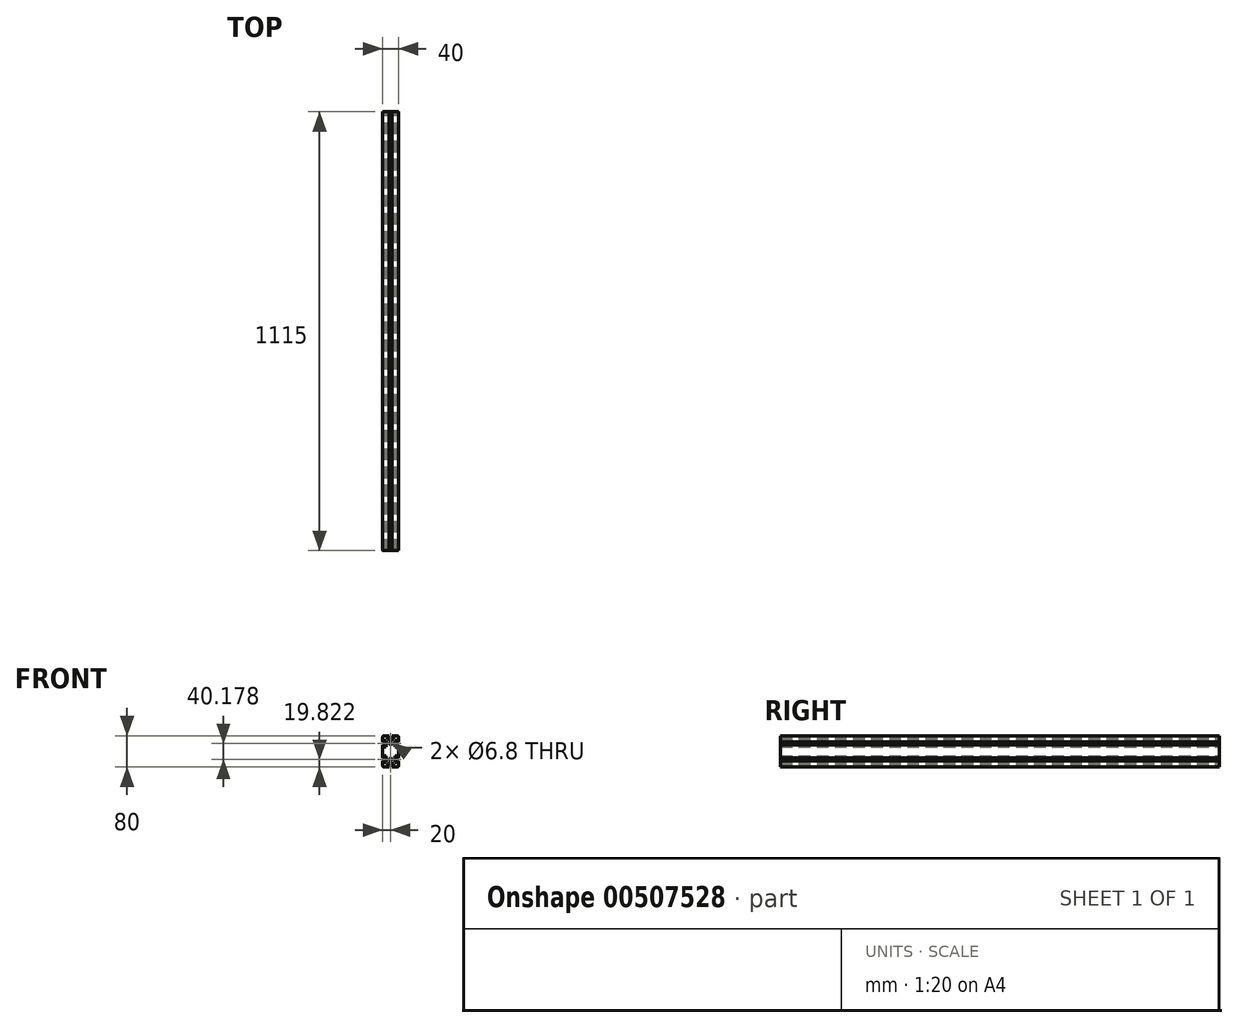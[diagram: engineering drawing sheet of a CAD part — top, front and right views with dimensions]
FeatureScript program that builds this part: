
annotation { "Feature Type Name" : "Feature", "Feature Type Description" : "" }
export const myFeature = defineFeature(function(context is Context, id is Id, definition is map)
    precondition{}
    {
        {
            var Q0;
            Q0=qCreatedBy(makeId("Front.planeOp"),FACE);
            var sketch = newSketch(context, id + "F0", { "sketchPlane" : qUnion([Q0])});
            skLineSegment(sketch, "E0", {"start": v(0, 4) * mm, "end": v(0, 16) * mm});
            skLineSegment(sketch, "E1", {"start": v(0, 16) * mm, "end": v(5, 16) * mm});
            skLineSegment(sketch, "E2", {"start": v(5, 16) * mm, "end": v(5, 11.64) * mm});
            skLineSegment(sketch, "E3", {"start": v(5, 11.64) * mm, "end": v(9, 11.64) * mm});
            skLineSegment(sketch, "E4", {"start": v(9, 11.64) * mm, "end": v(9, 28) * mm});
            skLineSegment(sketch, "E5", {"start": v(9, 28) * mm, "end": v(5, 28) * mm});
            skLineSegment(sketch, "E6", {"start": v(5, 28) * mm, "end": v(5, 24) * mm});
            skLineSegment(sketch, "E7", {"start": v(5, 24) * mm, "end": v(0, 24) * mm});
            skLineSegment(sketch, "E8", {"start": v(0, 24) * mm, "end": v(0, 56) * mm});
            skLineSegment(sketch, "E9", {"start": v(0, 56) * mm, "end": v(5, 56) * mm});
            skLineSegment(sketch, "E10", {"start": v(5, 56) * mm, "end": v(5, 52) * mm});
            skLineSegment(sketch, "E11", {"start": v(5, 52) * mm, "end": v(9, 52) * mm});
            skLineSegment(sketch, "E12", {"start": v(9, 52) * mm, "end": v(9, 68) * mm});
            skLineSegment(sketch, "E13", {"start": v(9, 68) * mm, "end": v(5, 68) * mm});
            skLineSegment(sketch, "E14", {"start": v(5, 68) * mm, "end": v(5, 64) * mm});
            skLineSegment(sketch, "E15", {"start": v(5, 64) * mm, "end": v(0, 64) * mm});
            skLineSegment(sketch, "E16", {"start": v(0, 64) * mm, "end": v(0, 76) * mm});
            skLineSegment(sketch, "E17", {"start": v(4, 80) * mm, "end": v(16, 80) * mm});
            skLineSegment(sketch, "E18", {"start": v(16, 80) * mm, "end": v(16, 75) * mm});
            skLineSegment(sketch, "E19", {"start": v(16, 75) * mm, "end": v(12, 75) * mm});
            skLineSegment(sketch, "E20", {"start": v(12, 75) * mm, "end": v(12, 71) * mm});
            skLineSegment(sketch, "E21", {"start": v(28, 75) * mm, "end": v(24, 75) * mm});
            skLineSegment(sketch, "E22", {"start": v(24, 75) * mm, "end": v(24, 80) * mm});
            skLineSegment(sketch, "E23", {"start": v(24, 80) * mm, "end": v(36, 80) * mm});
            skLineSegment(sketch, "E24", {"start": v(40, 76) * mm, "end": v(40, 64) * mm});
            skLineSegment(sketch, "E25", {"start": v(40, 64) * mm, "end": v(35, 64) * mm});
            skLineSegment(sketch, "E26", {"start": v(35, 64) * mm, "end": v(35, 68) * mm});
            skLineSegment(sketch, "E27", {"start": v(35, 68) * mm, "end": v(31, 68) * mm});
            skLineSegment(sketch, "E28", {"start": v(31, 68) * mm, "end": v(31, 52) * mm});
            skLineSegment(sketch, "E29", {"start": v(31, 52) * mm, "end": v(35, 52) * mm});
            skLineSegment(sketch, "E30", {"start": v(35, 52) * mm, "end": v(35, 56) * mm});
            skLineSegment(sketch, "E31", {"start": v(35, 56) * mm, "end": v(40, 56) * mm});
            skLineSegment(sketch, "E32", {"start": v(40, 56) * mm, "end": v(40, 24) * mm});
            skLineSegment(sketch, "E33", {"start": v(40, 24) * mm, "end": v(35, 24) * mm});
            skLineSegment(sketch, "E34", {"start": v(35, 24) * mm, "end": v(35, 28) * mm});
            skLineSegment(sketch, "E35", {"start": v(35, 28) * mm, "end": v(31, 28) * mm});
            skLineSegment(sketch, "E36", {"start": v(31, 28) * mm, "end": v(31, 11.64) * mm});
            skLineSegment(sketch, "E37", {"start": v(31, 11.64) * mm, "end": v(35, 11.64) * mm});
            skLineSegment(sketch, "E38", {"start": v(35, 11.64) * mm, "end": v(35, 16) * mm});
            skLineSegment(sketch, "E39", {"start": v(35, 16) * mm, "end": v(40, 16) * mm});
            skLineSegment(sketch, "E40", {"start": v(40, 16) * mm, "end": v(40, 4) * mm});
            skLineSegment(sketch, "E41", {"start": v(36, 0) * mm, "end": v(24, 0) * mm});
            skLineSegment(sketch, "E42", {"start": v(24, 0) * mm, "end": v(24, 5) * mm});
            skLineSegment(sketch, "E43", {"start": v(24, 5) * mm, "end": v(28, 5) * mm});
            skLineSegment(sketch, "E44", {"start": v(28, 5) * mm, "end": v(28, 9) * mm});
            skLineSegment(sketch, "E45", {"start": v(28, 9) * mm, "end": v(12, 9) * mm});
            skLineSegment(sketch, "E46", {"start": v(12, 9) * mm, "end": v(12, 5) * mm});
            skLineSegment(sketch, "E47", {"start": v(12, 5) * mm, "end": v(16, 5) * mm});
            skLineSegment(sketch, "E48", {"start": v(16, 5) * mm, "end": v(16, 0) * mm});
            skLineSegment(sketch, "E49", {"start": v(16, 0) * mm, "end": v(4, 0) * mm});
            skLineSegment(sketch, "E50", {"start": v(12, 71) * mm, "end": v(28, 71) * mm});
            skLineSegment(sketch, "E51", {"start": v(28, 71) * mm, "end": v(28, 75) * mm});
            skPoint(sketch, "E52.centerSnap0", {"position": v(20, 71) * mm});
            skPoint(sketch, "E52.centerSnap1", {"position": v(9, 60) * mm});
            skPoint(sketch, "E53.centerSnap0", {"position": v(9, 19.82) * mm});
            skPoint(sketch, "E53.centerSnap1", {"position": v(20, 9) * mm});
            skPoint(sketch, "E54.visualSharp", {"position": v(0, 80) * mm});
            skArc(sketch, "E54.filletArc", {"start": v(4, 80) * mm, "mid": v(1.17, 78.83) * mm, "end": v(0, 76) * mm});
            skPoint(sketch, "E55.visualSharp", {"position": v(40, 80) * mm});
            skArc(sketch, "E55.filletArc", {"start": v(40, 76) * mm, "mid": v(38.83, 78.83) * mm, "end": v(36, 80) * mm});
            skPoint(sketch, "E56.visualSharp", {"position": v(0, 0) * mm});
            skArc(sketch, "E56.filletArc", {"start": v(0, 4) * mm, "mid": v(1.17, 1.17) * mm, "end": v(4, 0) * mm});
            skPoint(sketch, "E57.visualSharp", {"position": v(40, 0) * mm});
            skArc(sketch, "E57.filletArc", {"start": v(36, 0) * mm, "mid": v(38.83, 1.17) * mm, "end": v(40, 4) * mm});
            skSolve(sketch);
        }
        {
            var Q0;
            Q0 = qSketchRegion(id + "F0", true);
            extrude(context, id + "F1", {"entities" : qUnion([Q0]), "depth" : 1115 * mm});
        }
        {
            var Q0;
            Q0=makeQuery(id+"F1.opExtrude","CAP_FACE",FACE,{"disambiguationData":[OSD([sQuery(id+"F0.wireOp",EDGE,"E0"),sQuery(id+"F0.wireOp",EDGE,"E1"),sQuery(id+"F0.wireOp",EDGE,"E2"),sQuery(id+"F0.wireOp",EDGE,"E3"),sQuery(id+"F0.wireOp",EDGE,"E4"),sQuery(id+"F0.wireOp",EDGE,"E5"),sQuery(id+"F0.wireOp",EDGE,"E6"),sQuery(id+"F0.wireOp",EDGE,"E7"),sQuery(id+"F0.wireOp",EDGE,"E8"),sQuery(id+"F0.wireOp",EDGE,"E9"),sQuery(id+"F0.wireOp",EDGE,"E10"),sQuery(id+"F0.wireOp",EDGE,"E11"),sQuery(id+"F0.wireOp",EDGE,"E12"),sQuery(id+"F0.wireOp",EDGE,"E13"),sQuery(id+"F0.wireOp",EDGE,"E14"),sQuery(id+"F0.wireOp",EDGE,"E15"),sQuery(id+"F0.wireOp",EDGE,"E16"),sQuery(id+"F0.wireOp",EDGE,"E17"),sQuery(id+"F0.wireOp",EDGE,"E18"),sQuery(id+"F0.wireOp",EDGE,"E19"),sQuery(id+"F0.wireOp",EDGE,"E20"),sQuery(id+"F0.wireOp",EDGE,"E21"),sQuery(id+"F0.wireOp",EDGE,"E22"),sQuery(id+"F0.wireOp",EDGE,"E23"),sQuery(id+"F0.wireOp",EDGE,"E24"),sQuery(id+"F0.wireOp",EDGE,"E25"),sQuery(id+"F0.wireOp",EDGE,"E26"),sQuery(id+"F0.wireOp",EDGE,"E27"),sQuery(id+"F0.wireOp",EDGE,"E28"),sQuery(id+"F0.wireOp",EDGE,"E29"),sQuery(id+"F0.wireOp",EDGE,"E30"),sQuery(id+"F0.wireOp",EDGE,"E31"),sQuery(id+"F0.wireOp",EDGE,"E32"),sQuery(id+"F0.wireOp",EDGE,"E33"),sQuery(id+"F0.wireOp",EDGE,"E34"),sQuery(id+"F0.wireOp",EDGE,"E35"),sQuery(id+"F0.wireOp",EDGE,"E36"),sQuery(id+"F0.wireOp",EDGE,"E37"),sQuery(id+"F0.wireOp",EDGE,"E38"),sQuery(id+"F0.wireOp",EDGE,"E39"),sQuery(id+"F0.wireOp",EDGE,"E40"),sQuery(id+"F0.wireOp",EDGE,"E41"),sQuery(id+"F0.wireOp",EDGE,"E42"),sQuery(id+"F0.wireOp",EDGE,"E43"),sQuery(id+"F0.wireOp",EDGE,"E44"),sQuery(id+"F0.wireOp",EDGE,"E45"),sQuery(id+"F0.wireOp",EDGE,"E46"),sQuery(id+"F0.wireOp",EDGE,"E47"),sQuery(id+"F0.wireOp",EDGE,"E48"),sQuery(id+"F0.wireOp",EDGE,"E49"),sQuery(id+"F0.wireOp",EDGE,"E50"),sQuery(id+"F0.wireOp",EDGE,"E51"),sQuery(id+"F0.wireOp",EDGE,"E54.filletArc"),sQuery(id+"F0.wireOp",EDGE,"E55.filletArc"),sQuery(id+"F0.wireOp",EDGE,"E56.filletArc"),sQuery(id+"F0.wireOp",EDGE,"E57.filletArc")])],"isStart":false});
            var sketch = newSketch(context, id + "F2", { "sketchPlane" : qUnion([Q0])});
            skCircle(sketch, "E58", {"center": v(20, 60) * mm, "radius": 3.4 * mm});
            skPoint(sketch, "E58.centerSnap0", {"position": v(20, 71) * mm});
            skPoint(sketch, "E58.centerSnap1", {"position": v(9, 60) * mm});
            skCircle(sketch, "E59", {"center": v(20, 19.82) * mm, "radius": 3.4 * mm});
            skPoint(sketch, "E59.centerSnap0", {"position": v(9, 19.82) * mm});
            skPoint(sketch, "E59.centerSnap1", {"position": v(20, 9) * mm});
            skSolve(sketch);
        }
        {
            var Q0;
            Q0 = qSketchRegion(id + "F2", true);
            extrude(context, id + "F3", {"entities" : qUnion([Q0]), "operationType" : NewBodyOperationType.REMOVE, "oppositeDirection" : true, "depth" : 1115 * mm});
        }
    });
